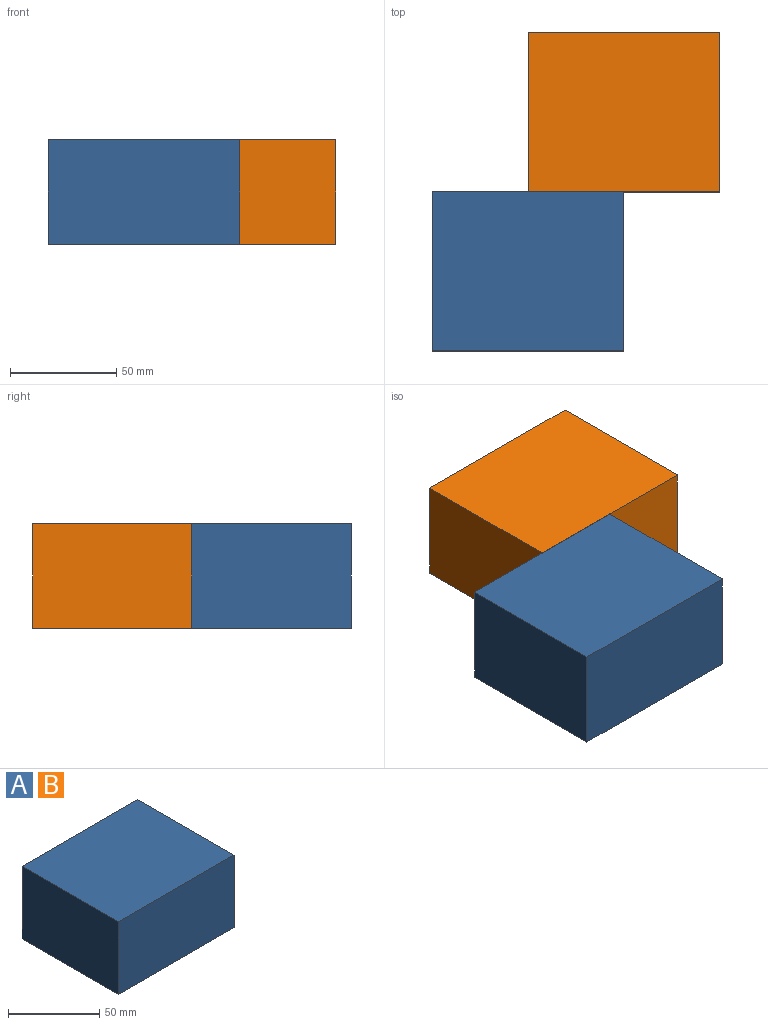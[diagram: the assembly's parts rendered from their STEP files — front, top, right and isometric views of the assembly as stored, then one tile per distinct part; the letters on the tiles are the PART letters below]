
ASSEMBLY  parts=2 mates=1
PART A: 6 faces, bbox 89.9x74.7x48.9 mm
  f0: plane 89.86x74.68mm, normal (0,0,1), area 6710.2mm2, adj f1,f3,f4,f5
  f1: plane 74.68x48.86mm, normal (-1,0,0), area 3648.5mm2, adj f0,f2,f4,f5
  f2: plane 89.86x74.68mm, normal (0,0,-1), area 6710.2mm2, adj f1,f3,f4,f5
  f3: plane 74.68x48.86mm, normal (1,0,0), area 3648.5mm2, adj f0,f2,f4,f5
  f4: plane 89.86x48.86mm, normal (0,-1,0), area 4390.2mm2, adj f0,f1,f2,f3
  f5: plane 89.86x48.86mm, normal (0,1,0), area 4390.2mm2, adj f0,f1,f2,f3
PART B: same geometry as A
PLACE A t=(24.27,25.61,6.43)mm fixed
PLACE B t=(69.2,100.28,6.43)mm
MATE fastened B.f4 <-> A.f5  axis (0,-1,0) through (114.12,25.61,30.86)mm
